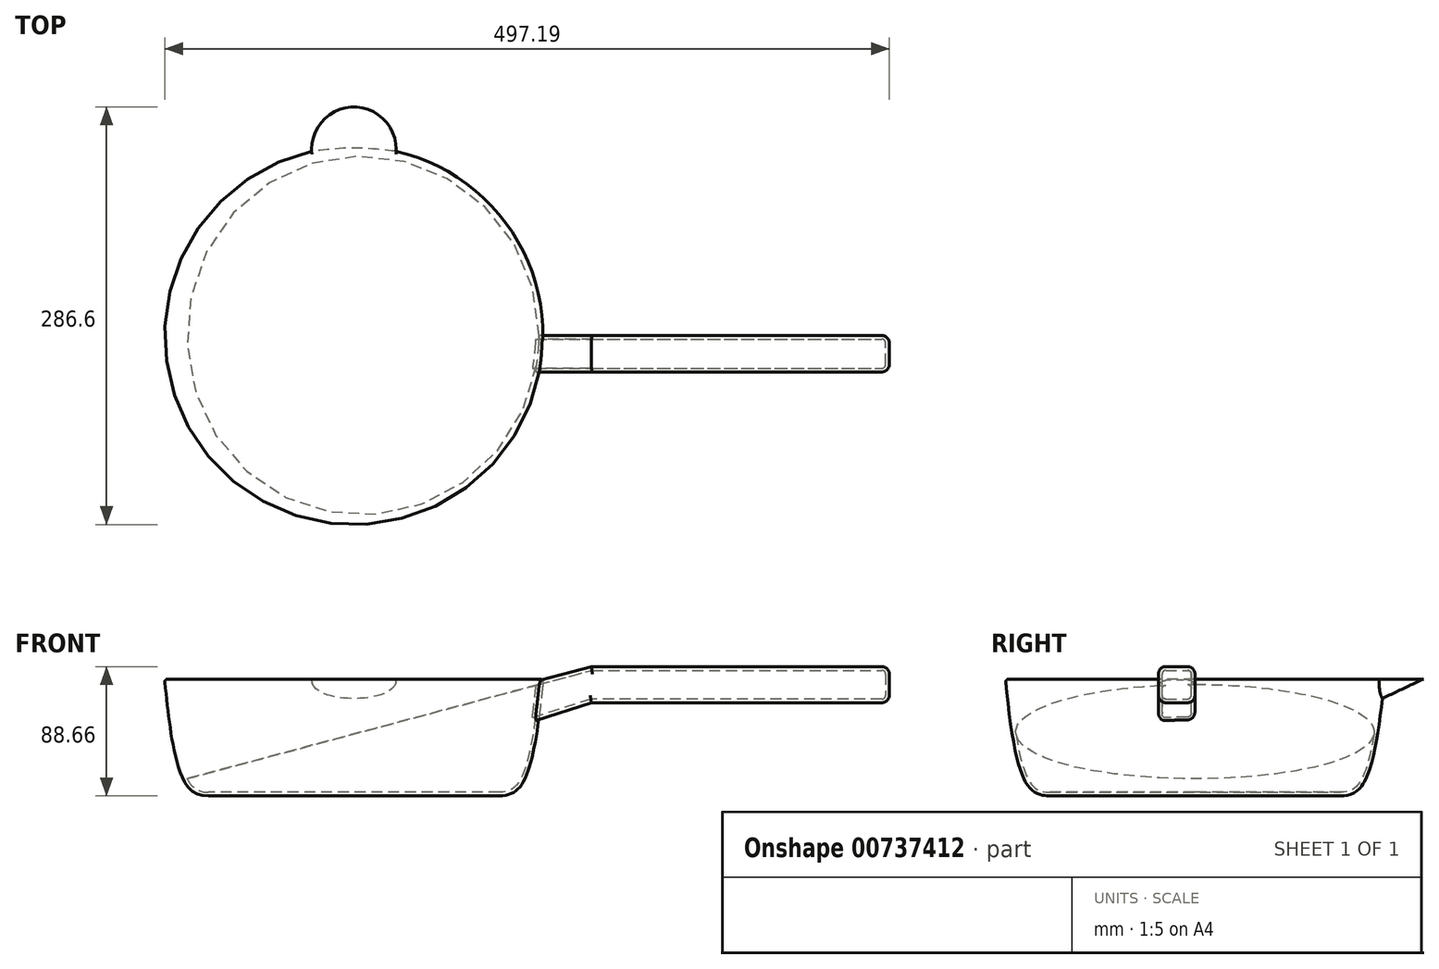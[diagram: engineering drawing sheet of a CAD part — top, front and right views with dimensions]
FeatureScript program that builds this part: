
annotation { "Feature Type Name" : "Feature", "Feature Type Description" : "" }
export const myFeature = defineFeature(function(context is Context, id is Id, definition is map)
    precondition{}
    {
        {
            var Q0;
            Q0=qCreatedBy(makeId("Front.planeOp"),FACE);
            var sketch = newSketch(context, id + "F0", { "sketchPlane" : qUnion([Q0])});
            skLineSegment(sketch, "E0", {"start": v(0, 0) * mm, "end": v(100, 0) * mm});
            skLineSegment(sketch, "E1", {"start": v(0, 0) * mm, "end": v(0, 80.15) * mm});
            skLineSegment(sketch, "E2", {"start": v(0, 80.15) * mm, "end": v(130, 80.15) * mm});
            skFitSpline(sketch, "E3", {"points": [v(130, 80.15) * mm, v(117.08, 11.12) * mm, v(100, 0) * mm], "startDerivative": vector(-11.25, -109.61) * mm, "endDerivative": vector(-68.06, 0) * mm});
            skSolve(sketch);
        }
        {
            var Q0;
            Q0=makeQuery(id+"F0.imprint","IMPRINT",FACE,{"disambiguationData":[TD([[makeQuery(id+"F0.imprint","IMPRINT",EDGE,{"derivedFrom":sQuery(id+"F0.wireOp",EDGE,"E0")}),1.0]])]});
            var Q1;
            Q1=sQuery(id+"F0.wireOp",EDGE,"E1");
            revolve(context, id + "F1", {"surfaceOperationType" : NewSurfaceOperationType.NEW, "entities" : qUnion([Q0]), "axis" : qUnion([Q1]), "revolveType" : RevolveType.FULL});
        }
        {
            var Q0;
            Q0=makeQuery(id+"F1.opRevolve","SWEPT_EDGE",EDGE,{"disambiguationData":[OSD([sQuery(id+"F0.wireOp",EDGE,"E2"),sQuery(id+"F0.wireOp",EDGE,"E3")])]});
            fillet(context, id + "F2", {"entities" : qUnion([Q0]), "radius" : 2 * mm, "tangentPropagation" : true, "allowEdgeOverflow" : false});
        }
        {
            var Q0;
            Q0=qCreatedBy(makeId("Front.planeOp"),FACE);
            var sketch = newSketch(context, id + "F3", { "sketchPlane" : qUnion([Q0])});
            skLineSegment(sketch, "E4", {"start": v(123, 77.94) * mm, "end": v(163, 88.66) * mm});
            skLineSegment(sketch, "E5", {"start": v(163, 88.66) * mm, "end": v(367.4, 88.66) * mm});
            skLineSegment(sketch, "E6", {"start": v(367.4, 88.66) * mm, "end": v(367.4, 63.94) * mm});
            skLineSegment(sketch, "E7", {"start": v(367.4, 63.94) * mm, "end": v(163, 63.94) * mm});
            skLineSegment(sketch, "E8", {"start": v(163, 63.94) * mm, "end": v(123, 50.94) * mm});
            skLineSegment(sketch, "E9", {"start": v(123, 50.94) * mm, "end": v(123, 77.94) * mm});
            skSolve(sketch);
        }
        {
            var Q0;
            Q0=makeQuery(id+"F3.imprint","IMPRINT",FACE,{"disambiguationData":[TD([[makeQuery(id+"F3.imprint","IMPRINT",EDGE,{"derivedFrom":sQuery(id+"F3.wireOp",EDGE,"E4")}),-1.0]])]});
            extrude(context, id + "F4", {"entities" : qUnion([Q0]), "operationType" : NewBodyOperationType.ADD, "depth" : 25 * mm, "offsetDistance" : 25 * mm});
        }
        {
            var Q0;
            Q0=makeQuery(id+"F4.opExtrude","CAP_EDGE",EDGE,{"disambiguationData":[OSD([sQuery(id+"F3.wireOp",EDGE,"E5")])],"isStart":false});
            var Q1;
            Q1=makeQuery(id+"F4.opExtrude","CAP_EDGE",EDGE,{"disambiguationData":[OSD([sQuery(id+"F3.wireOp",EDGE,"E7")])],"isStart":false});
            var Q2;
            Q2=makeQuery(id+"F4.opExtrude","CAP_EDGE",EDGE,{"disambiguationData":[OSD([sQuery(id+"F3.wireOp",EDGE,"E5")])],"isStart":true});
            var Q3;
            Q3=makeQuery(id+"F4.opExtrude","CAP_EDGE",EDGE,{"disambiguationData":[OSD([sQuery(id+"F3.wireOp",EDGE,"E7")])],"isStart":true});
            var Q4;
            Q4=makeQuery(id+"F4.opExtrude","CAP_EDGE",EDGE,{"disambiguationData":[OSD([sQuery(id+"F3.wireOp",EDGE,"E4")])],"isStart":false});
            var Q5;
            Q5=makeQuery(id+"F4.opExtrude","CAP_EDGE",EDGE,{"disambiguationData":[OSD([sQuery(id+"F3.wireOp",EDGE,"E4")])],"isStart":true});
            var Q6;
            Q6=makeQuery(id+"F4.opExtrude","CAP_EDGE",EDGE,{"disambiguationData":[OSD([sQuery(id+"F3.wireOp",EDGE,"E8")])],"isStart":false});
            var Q7;
            Q7=makeQuery(id+"F4.opExtrude","CAP_EDGE",EDGE,{"disambiguationData":[OSD([sQuery(id+"F3.wireOp",EDGE,"E8")])],"isStart":true});
            var Q8;
            Q8=makeQuery(id+"F4.opExtrude","SWEPT_EDGE",EDGE,{"disambiguationData":[OSD([sQuery(id+"F3.wireOp",EDGE,"E5"),sQuery(id+"F3.wireOp",EDGE,"E6")])]});
            var Q9;
            Q9=makeQuery(id+"F4.opExtrude","CAP_EDGE",EDGE,{"disambiguationData":[OSD([sQuery(id+"F3.wireOp",EDGE,"E6")])],"isStart":false});
            var Q10;
            Q10=makeQuery(id+"F4.opExtrude","SWEPT_EDGE",EDGE,{"disambiguationData":[OSD([sQuery(id+"F3.wireOp",EDGE,"E6"),sQuery(id+"F3.wireOp",EDGE,"E7")])]});
            var Q11;
            Q11=makeQuery(id+"F4.opExtrude","SWEPT_FACE",FACE,{"disambiguationData":[OSD([sQuery(id+"F3.wireOp",EDGE,"E6")])]});
            fillet(context, id + "F5", {"entities" : qUnion([Q0, Q1, Q2, Q3, Q4, Q5, Q6, Q7, Q8, Q9, Q10, Q11]), "radius" : 5 * mm, "tangentPropagation" : true, "allowEdgeOverflow" : false});
        }
        {
            var Q0;
            Q0=makeQuery(id+"F1.opRevolve","SWEPT_FACE",FACE,{"disambiguationData":[OSD([sQuery(id+"F0.wireOp",EDGE,"E2")])]});
            var sketch = newSketch(context, id + "F6", { "sketchPlane" : qUnion([Q0])});
            skArc(sketch, "E10", {"start": v(-28.85, 124.48) * mm, "mid": v(0, 156.82) * mm, "end": v(28.85, 124.48) * mm});
            skLineSegment(sketch, "E11", {"start": v(-41.7, 0) * mm, "end": v(41.17, 0) * mm});
            skLineSegment(sketch, "E12", {"start": v(41.17, 0) * mm, "end": v(28.85, 124.48) * mm});
            skLineSegment(sketch, "E13", {"start": v(-28.85, 124.48) * mm, "end": v(-41.7, 0) * mm});
            skSolve(sketch);
        }
        {
            var Q0;
            Q0=qCreatedBy(makeId("Right.planeOp"),FACE);
            var sketch = newSketch(context, id + "F7", { "sketchPlane" : qUnion([Q0])});
            skLineSegment(sketch, "E14", {"start": v(0, 80.15) * mm, "end": v(-91, 37.03) * mm});
            skSolve(sketch);
        }
        {
            var Q0;
            Q0 = qSketchRegion(id + "F6", true);
            var Q1;
            Q1 = qConstructionFilter(qBodyType(qCreatedBy(id + "F7" ,EDGE), BodyType.WIRE), ConstructionObject.NO);
            sweep(context, id + "F8", {"operationType" : NewBodyOperationType.ADD, "profiles" : qUnion([Q0]), "path" : qUnion([Q1])});
        }
        {
            var Q0;
            Q0=makeQuery(id+"F8.boolean.opBoolean","MERGE",FACE,{"derivedFrom":[makeQuery(id+"F1.opRevolve","SWEPT_FACE",FACE,{"disambiguationData":[OSD([sQuery(id+"F0.wireOp",EDGE,"E2")])]}),makeQuery(id+"F8.opSweep","CAP_FACE",FACE,{"disambiguationData":[OSD([sQuery(id+"F6.wireOp",EDGE,"E10"),sQuery(id+"F6.wireOp",EDGE,"E11"),sQuery(id+"F6.wireOp",EDGE,"E12"),sQuery(id+"F6.wireOp",EDGE,"E13"),sQuery(id+"F7.wireOp",VERTEX,"E14.start")])],"isStart":true})]});
            shell(context, id + "F9", {"entities" : qUnion([Q0]), "thickness" : 2.5 * mm});
        }
    });
